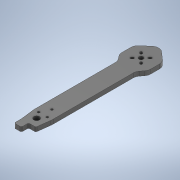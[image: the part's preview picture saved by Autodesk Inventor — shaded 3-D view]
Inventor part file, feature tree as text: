
AUTODESK INVENTOR PART (.ipt)
format: ipt  version: 2020 (Build 240168000, 168)  size: 186,880 bytes
history: native  units: in
note: dims shown in document units (in); Inventor stores cm internally (conversion verified against a paired STEP export)
features: sketch x1, projected_geometry x1
ambient origin geometry x8: Origin, YZ Plane, XZ Plane, XY Plane, X Axis, Y Axis, Z Axis, Center Point
bodies: Solid2 (feature_tree), Solid1 (feature_tree)
feature tree (2):
  sketch  "Sketch1"
  projected_geometry  "Projected Loop1"
